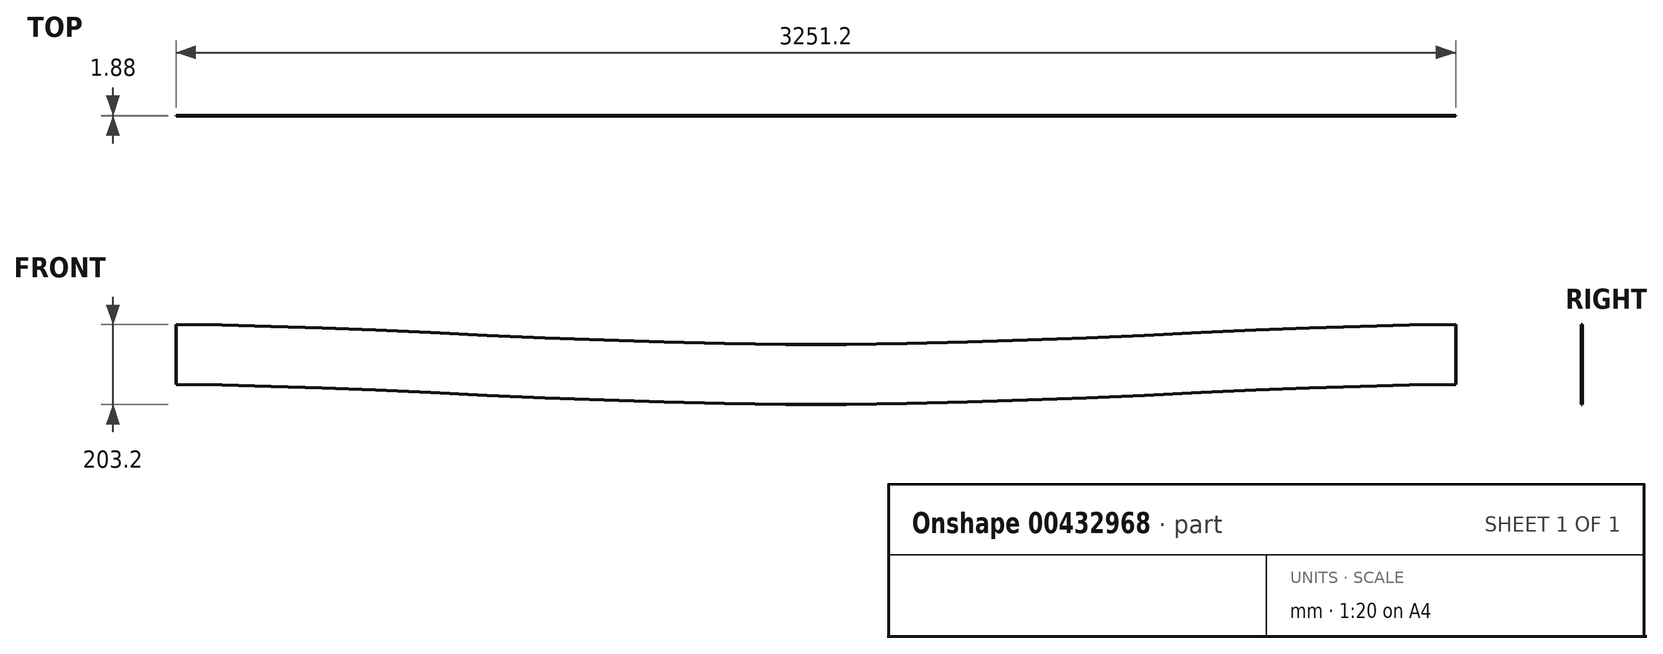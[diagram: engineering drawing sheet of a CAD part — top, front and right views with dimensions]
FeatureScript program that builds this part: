
annotation { "Feature Type Name" : "Feature", "Feature Type Description" : "" }
export const myFeature = defineFeature(function(context is Context, id is Id, definition is map)
    precondition{}
    {
        {
            assignVariable(context, id + "F0", {"name" : "width", "anyValue" : 1.88});
        }
        {
            var Q0;
            Q0=qCreatedBy(makeId("Front.planeOp"),FACE);
            var sketch = newSketch(context, id + "F1", { "sketchPlane" : qUnion([Q0])});
            skLineSegment(sketch, "E0.bottom", {"start": v(-1625.6, 76.2) * mm, "end": v(1625.6, 76.2) * mm, "construction": true});
            skLineSegment(sketch, "E0.top", {"start": v(-1625.6, -76.2) * mm, "end": v(1625.6, -76.2) * mm, "construction": true});
            skLineSegment(sketch, "E0.left", {"start": v(-1625.6, 76.2) * mm, "end": v(-1625.6, -76.2) * mm, "construction": true});
            skLineSegment(sketch, "E0.right", {"start": v(1625.6, 76.2) * mm, "end": v(1625.6, -76.2) * mm, "construction": true});
            skPoint(sketch, "E0.middle", {"position": v(0, 0) * mm});
            skLineSegment(sketch, "E1", {"start": v(0, 0) * mm, "end": v(0, 393.01) * mm, "construction": true});
            skLineSegment(sketch, "E2", {"start": v(-1625.6, 0) * mm, "end": v(1625.6, 0) * mm, "construction": true});
            skLineSegment(sketch, "E3", {"start": v(1625.6, 76.2) * mm, "end": v(1921.2, 76.2) * mm, "construction": true});
            skLineSegment(sketch, "E4.MirrorCS", {"start": v(-1625.6, 76.2) * mm, "end": v(-1921.2, 76.2) * mm, "construction": true});
            skLineSegment(sketch, "E5", {"start": v(1625.6, -76.2) * mm, "end": v(1921.2, -76.2) * mm, "construction": true});
            skLineSegment(sketch, "E6", {"start": v(-1625.6, -76.2) * mm, "end": v(-1921.2, -76.2) * mm, "construction": true});
            skFitSpline(sketch, "E7", {"points": [v(-1625.6, -76.2) * mm, v(0, -127) * mm, v(1625.6, -76.2) * mm], "startDerivative": vector(2625.3, 0) * mm, "endDerivative": vector(2625.3, 0) * mm});
            skFitSpline(sketch, "E8", {"points": [v(-1625.6, 76.2) * mm, v(0, 25.4) * mm, v(1625.6, 76.2) * mm], "startDerivative": vector(2625.3, 0) * mm, "endDerivative": vector(2625.3, 0) * mm});
            skLineSegment(sketch, "E9", {"start": v(0, 25.4) * mm, "end": v(0, -127) * mm, "construction": true});
            skLineSegment(sketch, "E10", {"start": v(-1625.6, 76.2) * mm, "end": v(-1625.6, -76.2) * mm});
            skLineSegment(sketch, "E11", {"start": v(1625.6, 76.2) * mm, "end": v(1625.6, -76.2) * mm});
            skSolve(sketch);
        }
        {
            var Q0;
            Q0=makeQuery(id+"F1.imprint","IMPRINT",FACE,{"disambiguationData":[TD([[makeQuery(id+"F1.imprint","IMPRINT",EDGE,{"derivedFrom":sQuery(id+"F1.wireOp",EDGE,"E7")}),1.0]])]});
            extrude(context, id + "F2", {"entities" : qUnion([Q0]), "depth" : (getVariable(context, 'width')) * mm, "symmetric" : true});
        }
    });
